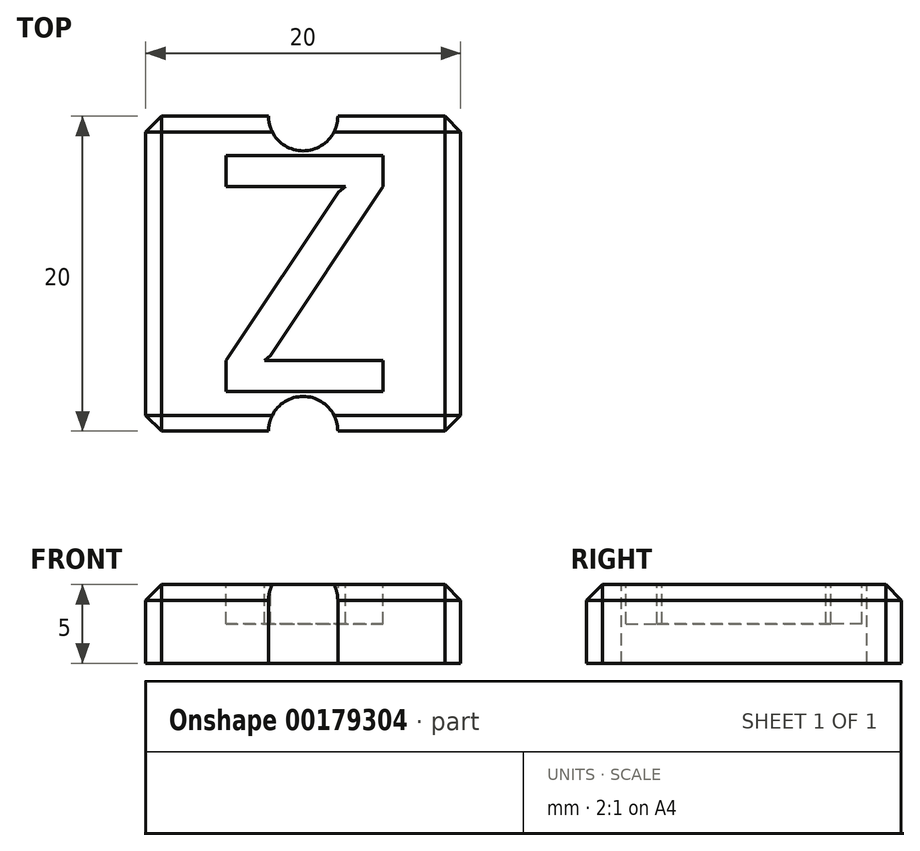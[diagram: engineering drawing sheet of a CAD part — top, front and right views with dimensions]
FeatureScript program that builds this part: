
annotation { "Feature Type Name" : "Feature", "Feature Type Description" : "" }
export const myFeature = defineFeature(function(context is Context, id is Id, definition is map)
    precondition{}
    {
        {
            var Q0;
            Q0=qCreatedBy(makeId("Top.planeOp"),FACE);
            var sketch = newSketch(context, id + "F0", { "sketchPlane" : qUnion([Q0])});
            skLineSegment(sketch, "E0.bottom", {"start": v(10, 8.66) * mm, "end": v(-10, 8.66) * mm});
            skLineSegment(sketch, "E0.top", {"start": v(10, -11.34) * mm, "end": v(-10, -11.34) * mm});
            skLineSegment(sketch, "E0.left", {"start": v(10, 8.66) * mm, "end": v(10, -11.34) * mm});
            skLineSegment(sketch, "E0.right", {"start": v(-10, 8.66) * mm, "end": v(-10, -11.34) * mm});
            skPoint(sketch, "E0.middle", {"position": v(0, -1.34) * mm});
            skArc(sketch, "E1", {"start": v(0, 12.66) * mm, "mid": v(2.83, 11.5) * mm, "end": v(4, 8.66) * mm});
            skPoint(sketch, "E1.startSnap0", {"position": v(0, 8.66) * mm});
            skArc(sketch, "E2", {"start": v(0, 12.66) * mm, "mid": v(-2.83, 11.5) * mm, "end": v(-4, 8.66) * mm});
            skArc(sketch, "E3", {"start": v(0, -15.34) * mm, "mid": v(-2.83, -14.17) * mm, "end": v(-4, -11.34) * mm});
            skPoint(sketch, "E3.startSnap0", {"position": v(0, -11.34) * mm});
            skArc(sketch, "E4", {"start": v(0, -15.34) * mm, "mid": v(2.83, -14.17) * mm, "end": v(4, -11.34) * mm});
            skSolve(sketch);
        }
        {
            var Q0;
            Q0=makeQuery(id+"F0.imprint","IMPRINT",FACE,{"disambiguationData":[TD([[makeQuery(id+"F0.imprint","IMPRINT",EDGE,{"derivedFrom":sQuery(id+"F0.wireOp",EDGE,"E0.bottom")}),1.0]])]});
            var Q1;
            {var subQ0=sQuery(id+"F0.wireOp",EDGE,"E1");Q1=makeQuery(id+"F0.imprint","IMPRINT",FACE,{"disambiguationData":[TD([[makeQuery(id+"F0.imprint","IMPRINT",EDGE,{"derivedFrom":subQ0}),-1.0]])]});}
            var Q2;
            {var subQ0=sQuery(id+"F0.wireOp",EDGE,"E3");Q2=makeQuery(id+"F0.imprint","IMPRINT",FACE,{"disambiguationData":[TD([[makeQuery(id+"F0.imprint","IMPRINT",EDGE,{"derivedFrom":subQ0}),-1.0]])]});}
            extrude(context, id + "F1", {"entities" : qUnion([Q0, Q1, Q2]), "depth" : 5 * mm});
        }
        {
            var Q0;
            Q0=makeQuery(id+"F1.opExtrude","CAP_FACE",FACE,{"disambiguationData":[OSD([sQuery(id+"F0.wireOp",EDGE,"E0.bottom"),sQuery(id+"F0.wireOp",EDGE,"E0.top"),sQuery(id+"F0.wireOp",EDGE,"E0.left"),sQuery(id+"F0.wireOp",EDGE,"E0.right")])],"isStart":false});
            var sketch = newSketch(context, id + "F2", { "sketchPlane" : qUnion([Q0])});
            skText(sketch, "E5", { "text": "Z", "fontName": "AllertaStencil-Regular.ttf"});
            skLineSegment(sketch, "E6", {"start": v(-4, 8.66) * mm, "end": v(4, 8.66) * mm, "construction": true});
            skPoint(sketch, "E7", {"position": v(0, 8.66) * mm});
            skLineSegment(sketch, "E8", {"start": v(-4, -11.34) * mm, "end": v(4, -11.34) * mm, "construction": true});
            skPoint(sketch, "E9", {"position": v(0, -11.34) * mm});
            const initialGuessF2  = {"E5": [-0.00647, -0.00884, 1, 0, 0.015]};
            skSetInitialGuess(sketch, initialGuessF2);
            skSolve(sketch);
        }
        {
            var Q0;
            Q0=makeQuery(id+"F2.imprint","IMPRINT",FACE,{"disambiguationData":[TD([[makeQuery(id+"F2.imprint","IMPRINT",EDGE,{"derivedFrom":sQuery(id+"F2.wireOp",EDGE,"E5.sketch_text.stroke-7")}),-1.0]])]});
            var Q1;
            Q1=makeQuery(id+"F2.imprint","IMPRINT",FACE,{"disambiguationData":[TD([[makeQuery(id+"F2.imprint","IMPRINT",EDGE,{"derivedFrom":sQuery(id+"F2.wireOp",EDGE,"E5.sketch_text.stroke-0")}),-1.0]])]});
            extrude(context, id + "F3", {"entities" : qUnion([Q0, Q1]), "operationType" : NewBodyOperationType.REMOVE, "oppositeDirection" : true, "depth" : 2.5 * mm});
        }
        {
            var Q0;
            Q0=sQuery(id+"F2.wireOp",VERTEX,"E7");
            var Q1;
            Q1=makeQuery(id+"F1.opExtrude","SWEPT_BODY",BODY,{"disambiguationData":[OSD([sQuery(id+"F0.wireOp",EDGE,"E0.bottom"),sQuery(id+"F0.wireOp",EDGE,"E0.top"),sQuery(id+"F0.wireOp",EDGE,"E0.left"),sQuery(id+"F0.wireOp",EDGE,"E0.right"),sQuery(id+"F0.wireOp",EDGE,"E1"),sQuery(id+"F0.wireOp",EDGE,"E2")])]});
            hole(context, id + "F4", {"style" : HoleStyle.SIMPLE, "endStyle" : HoleEndStyle.BLIND, "standardTappedOrClearance" : lookupTablePath({ "standard" : "ISO", "fit" : "Normal", "size" : "M4", "type" : "Clearance" }), "standardBlindInLast" : lookupTablePath({ "fit" : "Standard", "standard" : "ISO", "size" : "M4", "type" : "Clearance" }), "holeDiameter" : 4.4 * mm, "holeDepth" : 25 * mm, "locations" : qUnion([Q0]), "scope" : qUnion([Q1])});
        }
        {
            var Q0;
            Q0=sQuery(id+"F2.wireOp",VERTEX,"E9");
            var Q1;
            Q1=makeQuery(id+"F1.opExtrude","SWEPT_BODY",BODY,{"disambiguationData":[OSD([sQuery(id+"F0.wireOp",EDGE,"E0.bottom"),sQuery(id+"F0.wireOp",EDGE,"E0.top"),sQuery(id+"F0.wireOp",EDGE,"E0.left"),sQuery(id+"F0.wireOp",EDGE,"E0.right"),sQuery(id+"F0.wireOp",EDGE,"E1"),sQuery(id+"F0.wireOp",EDGE,"E2"),sQuery(id+"F0.wireOp",EDGE,"E3"),sQuery(id+"F0.wireOp",EDGE,"E4")])]});
            hole(context, id + "F5", {"style" : HoleStyle.SIMPLE, "endStyle" : HoleEndStyle.BLIND, "standardTappedOrClearance" : lookupTablePath({ "standard" : "ISO", "fit" : "Normal", "size" : "M4", "type" : "Clearance" }), "standardBlindInLast" : lookupTablePath({ "fit" : "Standard", "standard" : "ISO", "size" : "M4", "type" : "Clearance" }), "holeDiameter" : 4.4 * mm, "holeDepth" : 25 * mm, "locations" : qUnion([Q0]), "scope" : qUnion([Q1])});
        }
        {
            var Q0;
            Q0=makeQuery(id+"F1.opExtrude","SWEPT_EDGE",EDGE,{"disambiguationData":[OSD([sQuery(id+"F0.wireOp",EDGE,"E0.bottom"),sQuery(id+"F0.wireOp",EDGE,"E0.left")])]});
            var Q1;
            Q1=makeQuery(id+"F1.opExtrude","SWEPT_EDGE",EDGE,{"disambiguationData":[OSD([sQuery(id+"F0.wireOp",EDGE,"E0.top"),sQuery(id+"F0.wireOp",EDGE,"E0.left")])]});
            var Q2;
            Q2=makeQuery(id+"F1.opExtrude","SWEPT_EDGE",EDGE,{"disambiguationData":[OSD([sQuery(id+"F0.wireOp",EDGE,"E0.top"),sQuery(id+"F0.wireOp",EDGE,"E0.right")])]});
            var Q3;
            Q3=makeQuery(id+"F1.opExtrude","SWEPT_EDGE",EDGE,{"disambiguationData":[OSD([sQuery(id+"F0.wireOp",EDGE,"E0.bottom"),sQuery(id+"F0.wireOp",EDGE,"E0.right")])]});
            var Q4;
            Q4=makeQuery(id+"F1.opExtrude","CAP_EDGE",EDGE,{"disambiguationData":[OSD([sQuery(id+"F0.wireOp",EDGE,"E0.left")])],"isStart":false});
            var Q5;
            Q5=makeQuery(id+"F1.opExtrude","CAP_EDGE",EDGE,{"disambiguationData":[OSD([sQuery(id+"F0.wireOp",EDGE,"E0.right")])],"isStart":false});
            var Q6;
            {var subQ0=sQuery(id+"F0.wireOp",EDGE,"E0.bottom");Q6=makeQuery(id+"F1.opExtrude","CAP_EDGE",EDGE,{"disambiguationData":[OSD([subQ0]),TDD([makeQuery(id+"F0.imprint","IMPRINT",EDGE,{"disambiguationData":[TD([[makeQuery(id+"F0.imprint","INTERSECT",VERTEX,{"derivedFrom":[subQ0,sQuery(id+"F0.wireOp",EDGE,"E0.left")]}),-1.0]])],"derivedFrom":subQ0})])],"isStart":false});}
            var Q7;
            {var subQ0=sQuery(id+"F0.wireOp",EDGE,"E0.bottom");Q7=makeQuery(id+"F1.opExtrude","CAP_EDGE",EDGE,{"disambiguationData":[OSD([subQ0]),TDD([makeQuery(id+"F0.imprint","IMPRINT",EDGE,{"disambiguationData":[TD([[makeQuery(id+"F0.imprint","INTERSECT",VERTEX,{"derivedFrom":[subQ0,sQuery(id+"F0.wireOp",EDGE,"E0.right")]}),1.0]])],"derivedFrom":subQ0})])],"isStart":false});}
            var Q8;
            {var subQ0=sQuery(id+"F0.wireOp",EDGE,"E0.top");Q8=makeQuery(id+"F1.opExtrude","CAP_EDGE",EDGE,{"disambiguationData":[OSD([subQ0]),TDD([makeQuery(id+"F0.imprint","IMPRINT",EDGE,{"disambiguationData":[TD([[makeQuery(id+"F0.imprint","INTERSECT",VERTEX,{"derivedFrom":[subQ0,sQuery(id+"F0.wireOp",EDGE,"E0.left")]}),-1.0]])],"derivedFrom":subQ0})])],"isStart":false});}
            var Q9;
            {var subQ0=sQuery(id+"F0.wireOp",EDGE,"E0.top");Q9=makeQuery(id+"F1.opExtrude","CAP_EDGE",EDGE,{"disambiguationData":[OSD([subQ0]),TDD([makeQuery(id+"F0.imprint","IMPRINT",EDGE,{"disambiguationData":[TD([[makeQuery(id+"F0.imprint","INTERSECT",VERTEX,{"derivedFrom":[subQ0,sQuery(id+"F0.wireOp",EDGE,"E0.right")]}),1.0]])],"derivedFrom":subQ0})])],"isStart":false});}
            chamfer(context, id + "F6", {"entities" : qUnion([Q0, Q1, Q2, Q3, Q4, Q5, Q6, Q7, Q8, Q9]), "width" : 1 * mm, "tangentPropagation" : true});
        }
    });
